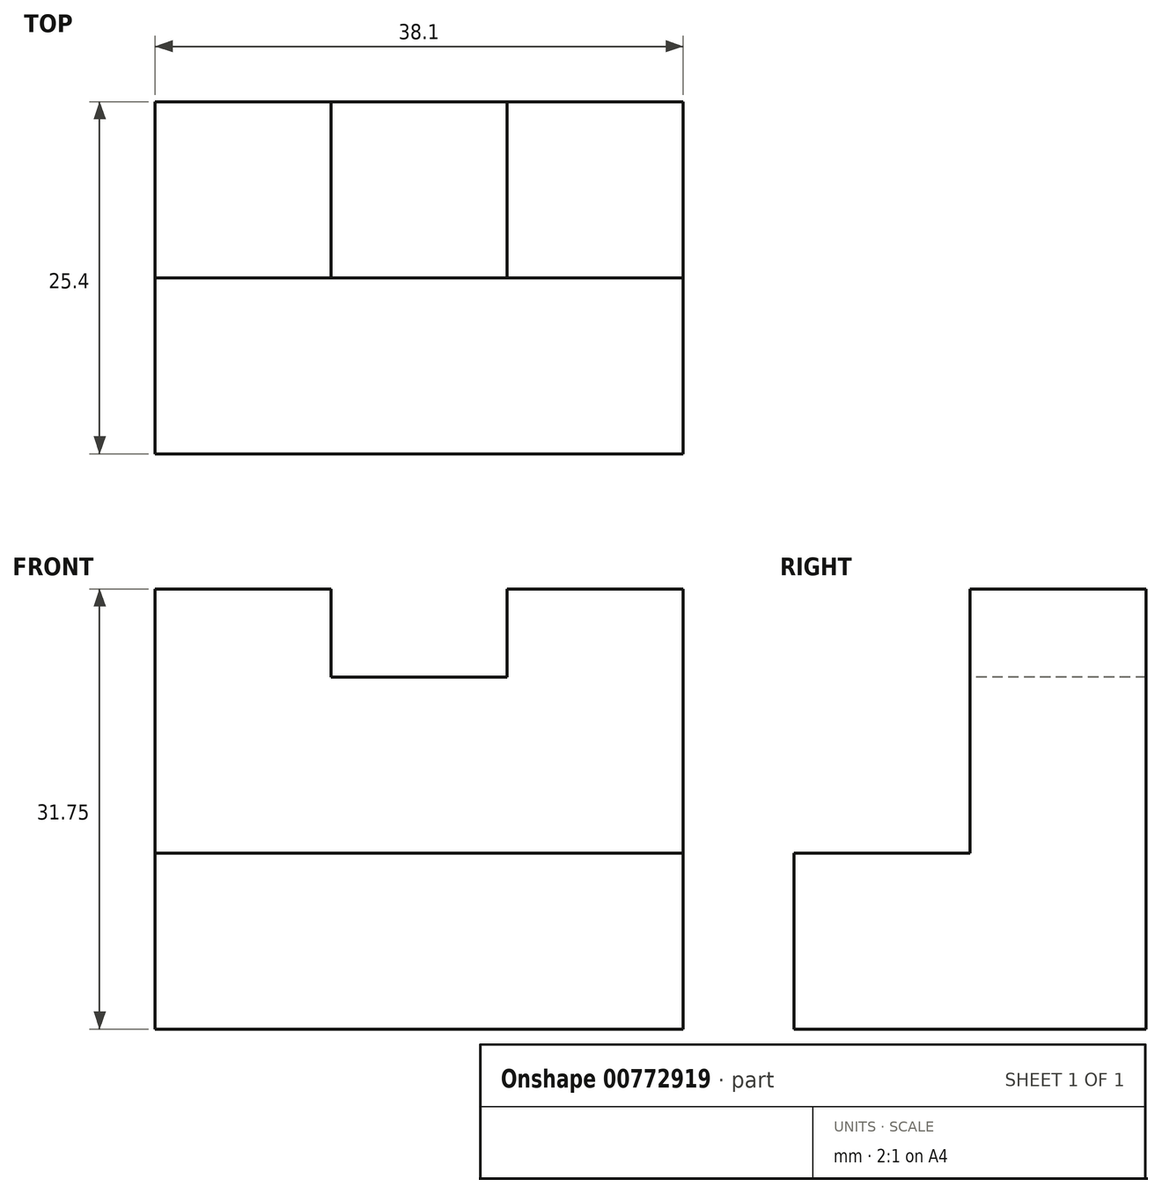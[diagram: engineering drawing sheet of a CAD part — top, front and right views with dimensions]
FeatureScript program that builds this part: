
annotation { "Feature Type Name" : "Feature", "Feature Type Description" : "" }
export const myFeature = defineFeature(function(context is Context, id is Id, definition is map)
    precondition{}
    {
        {
            var Q0;
            Q0=qCreatedBy(makeId("Right.planeOp"),FACE);
            var sketch = newSketch(context, id + "F0", { "sketchPlane" : qUnion([Q0])});
            skLineSegment(sketch, "E0", {"start": v(0, 0) * mm, "end": v(25.4, 0) * mm});
            skLineSegment(sketch, "E1", {"start": v(25.4, 0) * mm, "end": v(25.4, 31.75) * mm});
            skLineSegment(sketch, "E2", {"start": v(25.4, 31.75) * mm, "end": v(12.7, 31.75) * mm});
            skLineSegment(sketch, "E3", {"start": v(12.7, 31.75) * mm, "end": v(12.7, 12.7) * mm});
            skLineSegment(sketch, "E4", {"start": v(12.7, 12.7) * mm, "end": v(0, 12.7) * mm});
            skLineSegment(sketch, "E5", {"start": v(0, 12.7) * mm, "end": v(0, 0) * mm});
            skSolve(sketch);
        }
        {
            var Q0;
            Q0=makeQuery(id+"F0.imprint","IMPRINT",FACE,{"disambiguationData":[TD([[makeQuery(id+"F0.imprint","IMPRINT",EDGE,{"derivedFrom":sQuery(id+"F0.wireOp",EDGE,"E0")}),1.0]])]});
            extrude(context, id + "F1", {"entities" : qUnion([Q0]), "depth" : 38.1 * mm, "offsetDistance" : 25.4 * mm});
        }
        {
            var Q0;
            Q0=makeQuery(id+"F1.opExtrude","SWEPT_FACE",FACE,{"disambiguationData":[OSD([sQuery(id+"F0.wireOp",EDGE,"E2")])]});
            var sketch = newSketch(context, id + "F2", { "sketchPlane" : qUnion([Q0])});
            skLineSegment(sketch, "E6", {"start": v(0, 12.7) * mm, "end": v(12.7, 12.7) * mm});
            skLineSegment(sketch, "E7", {"start": v(38.1, 12.7) * mm, "end": v(25.4, 12.7) * mm});
            skLineSegment(sketch, "E8", {"start": v(0, 25.4) * mm, "end": v(12.7, 25.4) * mm});
            skLineSegment(sketch, "E9", {"start": v(12.7, 25.4) * mm, "end": v(12.7, 12.7) * mm});
            skLineSegment(sketch, "E10", {"start": v(25.4, 12.7) * mm, "end": v(25.4, 25.4) * mm});
            skLineSegment(sketch, "E11", {"start": v(25.4, 25.4) * mm, "end": v(38.1, 25.4) * mm});
            skSolve(sketch);
        }
        {
            var Q0;
            {var subQ0=sQuery(id+"F2.wireOp",EDGE,"E9");Q0=makeQuery(id+"F2.imprint","IMPRINT",FACE,{"disambiguationData":[TD([[makeQuery(id+"F2.imprint","IMPRINT",EDGE,{"derivedFrom":subQ0}),1.0]])]});}
            extrude(context, id + "F3", {"entities" : qUnion([Q0]), "operationType" : NewBodyOperationType.REMOVE, "oppositeDirection" : true, "depth" : 6.35 * mm, "offsetDistance" : 25.4 * mm});
        }
    });
